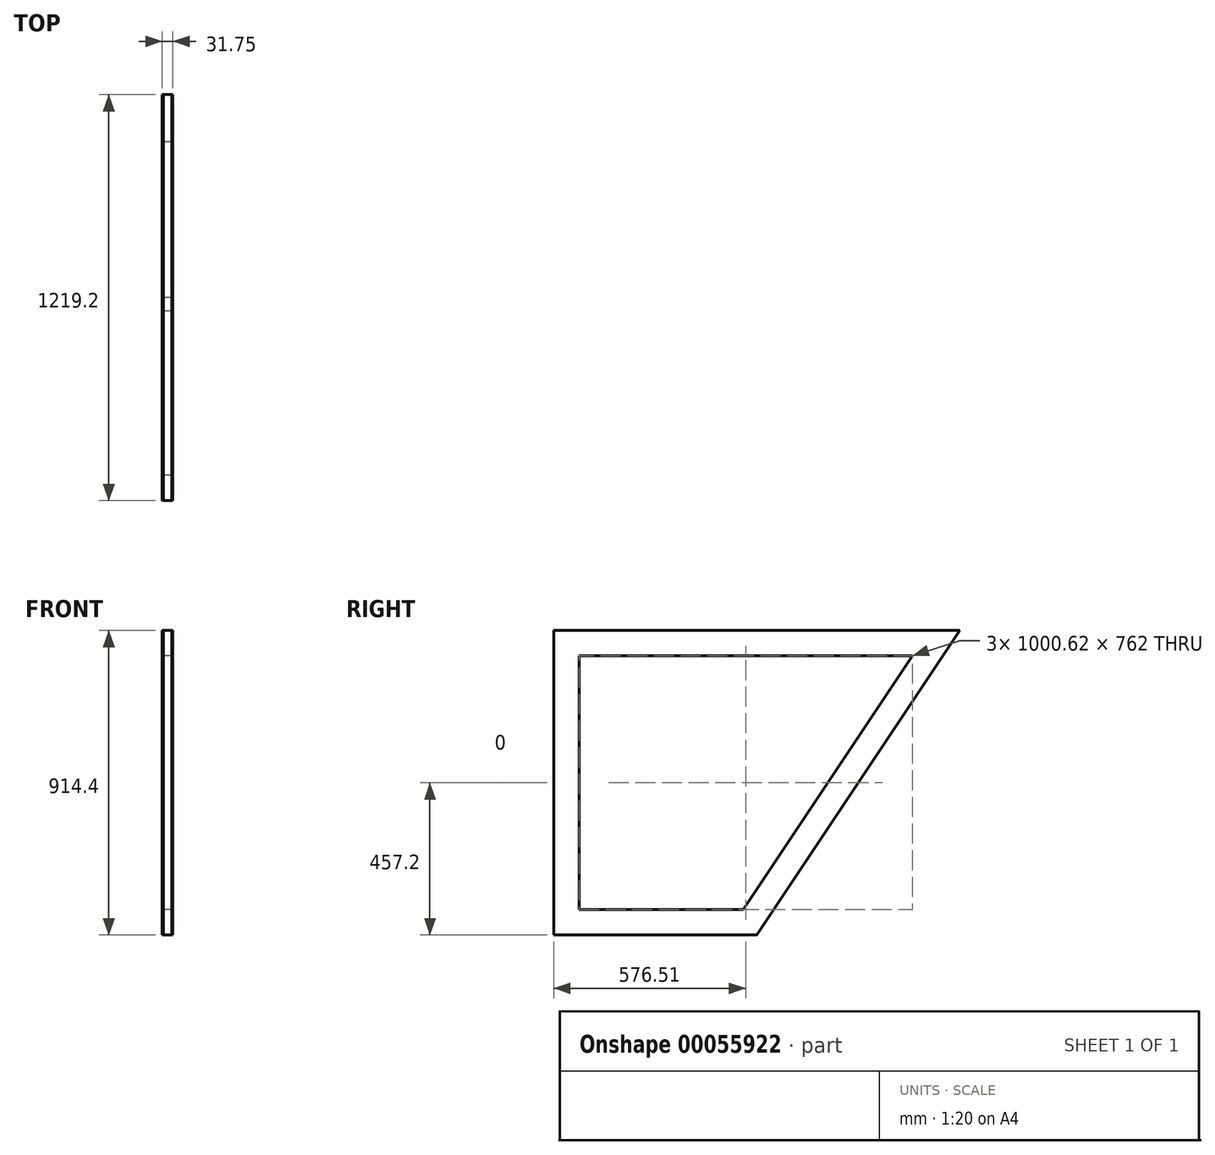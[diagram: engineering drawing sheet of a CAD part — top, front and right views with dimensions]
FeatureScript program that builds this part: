
annotation { "Feature Type Name" : "Feature", "Feature Type Description" : "" }
export const myFeature = defineFeature(function(context is Context, id is Id, definition is map)
    precondition{}
    {
        {
            var Q0;
            Q0=qCreatedBy(makeId("Right.planeOp"),FACE);
            var sketch = newSketch(context, id + "F0", { "sketchPlane" : qUnion([Q0])});
            skLineSegment(sketch, "E0", {"start": v(0, 0) * mm, "end": v(0, 914.4) * mm});
            skLineSegment(sketch, "E1", {"start": v(609.6, 0) * mm, "end": v(1219.2, 914.4) * mm});
            skLineSegment(sketch, "E2", {"start": v(0, 914.4) * mm, "end": v(1219.2, 914.4) * mm});
            skLineSegment(sketch, "E3", {"start": v(0, 0) * mm, "end": v(609.6, 0) * mm});
            skLineSegment(sketch, "E4.0", {"start": v(76.2, 838.2) * mm, "end": v(1076.82, 838.2) * mm});
            skLineSegment(sketch, "E4.1", {"start": v(76.2, 76.2) * mm, "end": v(76.2, 838.2) * mm});
            skLineSegment(sketch, "E4.2", {"start": v(76.2, 76.2) * mm, "end": v(568.82, 76.2) * mm});
            skLineSegment(sketch, "E4.3", {"start": v(568.82, 76.2) * mm, "end": v(1076.82, 838.2) * mm});
            skSolve(sketch);
        }
        {
            var Q0;
            Q0 = qSketchRegion(id + "F0", true);
            extrude(context, id + "F1", {"entities" : qUnion([Q0]), "depth" : 3.17 * mm});
        }
        {
            var Q0;
            Q0=makeQuery(id+"F1.opExtrude","CAP_FACE",FACE,{"disambiguationData":[OSD([sQuery(id+"F0.wireOp",EDGE,"E0"),sQuery(id+"F0.wireOp",EDGE,"E1"),sQuery(id+"F0.wireOp",EDGE,"E2"),sQuery(id+"F0.wireOp",EDGE,"E3"),sQuery(id+"F0.wireOp",EDGE,"E4.0"),sQuery(id+"F0.wireOp",EDGE,"E4.1"),sQuery(id+"F0.wireOp",EDGE,"E4.2"),sQuery(id+"F0.wireOp",EDGE,"E4.3")])],"isStart":false});
            var sketch = newSketch(context, id + "F2", { "sketchPlane" : qUnion([Q0])});
            skLineSegment(sketch, "E5", {"start": v(0, 914.4) * mm, "end": v(1219.2, 914.4) * mm});
            skLineSegment(sketch, "E6", {"start": v(1219.2, 914.4) * mm, "end": v(609.6, 0) * mm});
            skLineSegment(sketch, "E7", {"start": v(609.6, 0) * mm, "end": v(0, 0) * mm});
            skLineSegment(sketch, "E8", {"start": v(0, 0) * mm, "end": v(0, 914.4) * mm});
            skLineSegment(sketch, "E9", {"start": v(76.2, 838.2) * mm, "end": v(1076.82, 838.2) * mm});
            skLineSegment(sketch, "E10", {"start": v(1076.82, 838.2) * mm, "end": v(568.82, 76.2) * mm});
            skLineSegment(sketch, "E11", {"start": v(568.82, 76.2) * mm, "end": v(76.2, 76.2) * mm});
            skLineSegment(sketch, "E12", {"start": v(76.2, 76.2) * mm, "end": v(76.2, 838.2) * mm});
            skSolve(sketch);
        }
        {
            var Q0;
            Q0 = qSketchRegion(id + "F2", true);
            extrude(context, id + "F3", {"entities" : qUnion([Q0]), "depth" : 25.4 * mm});
        }
        {
            var Q0;
            Q0=makeQuery(id+"F3.opExtrude","CAP_FACE",FACE,{"disambiguationData":[OSD([sQuery(id+"F2.wireOp",EDGE,"E5"),sQuery(id+"F2.wireOp",EDGE,"E6"),sQuery(id+"F2.wireOp",EDGE,"E7"),sQuery(id+"F2.wireOp",EDGE,"E8"),sQuery(id+"F2.wireOp",EDGE,"E9"),sQuery(id+"F2.wireOp",EDGE,"E10"),sQuery(id+"F2.wireOp",EDGE,"E11"),sQuery(id+"F2.wireOp",EDGE,"E12")])],"isStart":false});
            var sketch = newSketch(context, id + "F4", { "sketchPlane" : qUnion([Q0])});
            skLineSegment(sketch, "E13", {"start": v(0, 914.4) * mm, "end": v(1219.2, 914.4) * mm});
            skLineSegment(sketch, "E14", {"start": v(1219.2, 914.4) * mm, "end": v(609.6, 0) * mm});
            skLineSegment(sketch, "E15", {"start": v(609.6, 0) * mm, "end": v(0, 0) * mm});
            skLineSegment(sketch, "E16", {"start": v(0, 0) * mm, "end": v(0, 914.4) * mm});
            skLineSegment(sketch, "E17", {"start": v(76.2, 838.2) * mm, "end": v(1076.82, 838.2) * mm});
            skLineSegment(sketch, "E18", {"start": v(1076.82, 838.2) * mm, "end": v(568.82, 76.2) * mm});
            skLineSegment(sketch, "E19", {"start": v(568.82, 76.2) * mm, "end": v(76.2, 76.2) * mm});
            skLineSegment(sketch, "E20", {"start": v(76.2, 76.2) * mm, "end": v(76.2, 838.2) * mm});
            skSolve(sketch);
        }
        {
            var Q0;
            Q0 = qSketchRegion(id + "F4", true);
            extrude(context, id + "F5", {"entities" : qUnion([Q0]), "depth" : 3.17 * mm});
        }
    });
